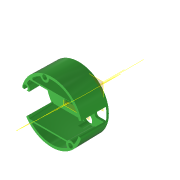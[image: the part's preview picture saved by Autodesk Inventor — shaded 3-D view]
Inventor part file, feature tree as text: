
AUTODESK INVENTOR PART (.ipt)
format: ipt  version: 2022 (Build 260153000, 153)  size: 645,120 bytes
history: native  units: in
note: dims shown in document units (in); Inventor stores cm internally (conversion verified against a paired STEP export)
features: extrude x14, sketch x14, other x11, reference x7, plane x6, projected_geometry x2, fillet x1
ambient origin geometry x8: Origin, YZ Plane, XZ Plane, XY Plane, X Axis, Y Axis, Z Axis, Center Point
bodies: Solid1 (feature_tree)
feature tree (55):
  plane  "Arbeitsebene6"
  extrude  "Extrusion1"  Depth=0.315in
  extrude  "Extrusion2"  Depth=1.0in
  plane  "Arbeitsebene3"
  extrude  "Extrusion6"  Depth=0.1102in
  plane  "Arbeitsebene2"
  extrude  "Extrusion7"  Depth=0.0787in
  extrude  "Extrusion10"  Depth=0.0394in TaperAngle=0.0deg
  plane  "Arbeitsebene7"
  sketch  "Skizze16"  dims[d81=0.0591in d82=0.3937in d83=0.0069in]
  plane  "Arbeitsebene5"
  extrude  "Extrusion14"  Depth=0.3937in
  extrude  "Extrusion15"  Depth=0.3937in
  extrude  "Extrusion17"  TaperAngle=0.0deg  [1 undecoded]
  extrude  "Extrusion18"  Depth=0.1575in
  extrude  "Extrusion19"  Depth=0.1575in
  extrude  "Extrusion20"  Depth=0.8465in TaperAngle=0.0deg
  fillet  "Rundung2"  Radius=0.1614in
  extrude  "Extrusion21"  Depth=0.1614in
  extrude  "Extrusion22"  Depth=0.315in
  extrude  "Extrusion23"  Depth=0.0591in
  plane  "Arbeitsebene8"
  sketch  "Sketch1"  dims[d0=0.0787in d1=-0.0069in d2=0.315in]
  sketch  "Sketch2"  dims[d3=0.3189in d4=1.0in d5=-0.0137in]
  sketch  "Sketch8"  dims[d33=0.1102in d34=0.1102in]
  sketch  "Sketch9"  dims[d35=0.0in d36=0.0in d37=0.0787in]
  sketch  "Skizze12"  dims[d38=0.0004in d39=-0.0069in d51=0.0394in d52=0.0in]
  sketch  "Skizze17"  dims[d89=0.3937in d90=-0.0069in d91=0.0787in]
  reference  "Referenz44"
  reference  "Referenz45"
  projected_geometry  "Projizierte Kontur4"
  sketch  "Skizze19"  dims[d92=0.0787in d93=0.0in]
  sketch  "Skizze20"  dims[d94=0.0in d104=0.1575in]
  sketch  "Skizze21"  dims[d105=0.1575in d106=0.1575in]
  sketch  "Skizze22"  dims[d107=0.0001in d108=-0.0069in d109=0.8465in d110=0.0in d111=0.1614in]
  reference  "Referenz46"
  sketch  "Skizze23"  dims[d112=0.1614in d113=0.1614in]
  sketch  "Skizze24"  dims[d114=0.1969in d115=-0.0069in d116=0.315in]
  projected_geometry  "Projizierte Kontur5"
  reference  "Referenz47"
  sketch  "Skizze25"  dims[d117=0.315in d118=0.0069in d119=0.0394in d120=0.0394in d122=0.9055in d123=0.4528in d124=1.8701in d125=0.2756in d126=0.4724in d127=0.5906in d128=0.0394in d129=0.0in d130=0.315in d131=0.315in d132=0.1102in d133=0.1102in d134=0.0in d135=0.0in d136=1.4961in d137=0.315in d138=0.315in d139=0.0591in d140=0.0in d78=0.0197in d79=0.0344in d80=0.0197in d95=0.0197in d96=0.0344in d97=0.0197in d98=0.0344in]
  reference  "Referenz48"
  reference  "Referenz49"
  reference  "Referenz50"
  other  "Arbeitsachse1"
  other  "Arbeitsachse2"
  other  "Matchboxscope_VCM_v1.iam"
  other  "Matchboxscope_bottom_v0:2"
  other  "Matchboxscope_middle2_m12VCMLens_v2:2"
  other  "Spectroscope_v0.iam"
  other  "IM_Matchboxscope_plate:1"
  other  "Assembly_Matchboxscope_injectionmolded_ESPectrometer.iam"
  other  "IM_Matchboxscope_plate:2"
  other  "IM_Lensholder:1"
  other  "DIN 912 - ersetzt durch DIN EN ISO 4762 M3 x 10:3"
note: 1 required parameter value undecoded (feature->parameter linkage not recoverable at this tier; creation-order binding heuristic only, values carry confidence <= 0.55)
